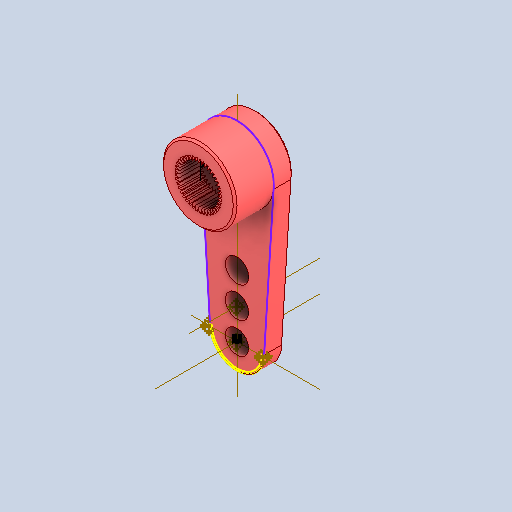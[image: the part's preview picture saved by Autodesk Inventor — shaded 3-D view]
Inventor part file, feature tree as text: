
AUTODESK INVENTOR PART (.ipt)
format: ipt  version: 2025.2 (Build 292293000, 293)  size: 422,912 bytes
history: native  units: in
note: dims shown in document units (in); Inventor stores cm internally (conversion verified against a paired STEP export)
features: other x17, sketch x1, chamfer x1
ambient origin geometry x8: Origin, YZ Plane, XZ Plane, XY Plane, X Axis, Y Axis, Z Axis, Center Point
bodies: Solid1 (feature_tree)
feature tree (19):
  other  "Annotations"
  other  "ServoAxis"
  other  "Work Axis2"
  other  "Work Point1"
  other  "Work Point2"
  other  "Work Axis3"
  other  "Work Point4"
  other  "Work Axis5"
  other  "Work Axis6"
  other  "Work Axis7"
  other  "Work Axis8"
  other  "Work Point5"
  other  "Work Point6"
  other  "Work Point7"
  sketch  "Sketch2"  dims[d0=0.187in]
  other  "Work Axis4"
  other  "Work Point3"
  chamfer  "Chamfer4"  [1 undecoded]
  other  "Linear Dimension 1"
note: 1 required parameter value undecoded (feature->parameter linkage not recoverable at this tier; creation-order binding heuristic only, values carry confidence <= 0.55)
